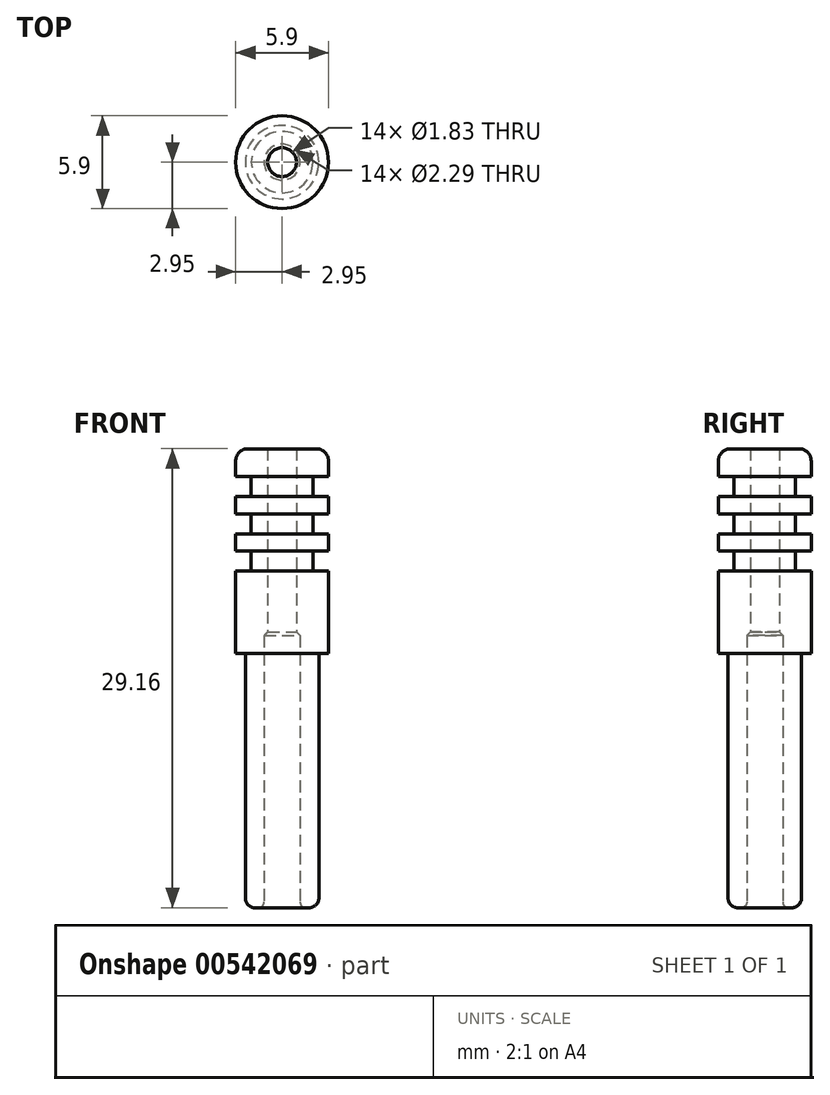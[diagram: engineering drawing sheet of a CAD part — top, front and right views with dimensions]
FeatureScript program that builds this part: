
annotation { "Feature Type Name" : "Feature", "Feature Type Description" : "" }
export const myFeature = defineFeature(function(context is Context, id is Id, definition is map)
    precondition{}
    {
        {
            var Q0;
            Q0=qCreatedBy(makeId("Front.planeOp"),FACE);
            var sketch = newSketch(context, id + "F0", { "sketchPlane" : qUnion([Q0])});
            skLineSegment(sketch, "E0", {"start": v(0.91, 1.37) * mm, "end": v(0.91, 13) * mm});
            skLineSegment(sketch, "E1", {"start": v(0.91, 13) * mm, "end": v(2.18, 13) * mm});
            skLineSegment(sketch, "E2", {"start": v(2.95, 12.24) * mm, "end": v(2.95, 11.25) * mm});
            skLineSegment(sketch, "E3", {"start": v(2.95, 11.25) * mm, "end": v(1.96, 11.25) * mm});
            skLineSegment(sketch, "E4", {"start": v(1.96, 11.25) * mm, "end": v(1.96, 9.98) * mm});
            skLineSegment(sketch, "E5", {"start": v(1.96, 9.98) * mm, "end": v(2.95, 9.98) * mm});
            skLineSegment(sketch, "E6", {"start": v(2.95, 9.98) * mm, "end": v(2.95, 8.86) * mm});
            skLineSegment(sketch, "E7", {"start": v(2.95, 8.87) * mm, "end": v(1.96, 8.87) * mm});
            skLineSegment(sketch, "E8", {"start": v(1.96, 8.87) * mm, "end": v(1.96, 7.6) * mm});
            skLineSegment(sketch, "E9", {"start": v(1.96, 7.6) * mm, "end": v(2.95, 7.6) * mm});
            skLineSegment(sketch, "E10", {"start": v(2.95, 7.6) * mm, "end": v(2.95, 6.5) * mm});
            skLineSegment(sketch, "E11", {"start": v(2.95, 6.5) * mm, "end": v(1.96, 6.5) * mm});
            skLineSegment(sketch, "E12", {"start": v(1.96, 6.5) * mm, "end": v(1.96, 5.23) * mm});
            skLineSegment(sketch, "E13", {"start": v(2.34, 0) * mm, "end": v(2.34, -15.52) * mm});
            skLineSegment(sketch, "E14", {"start": v(1.7, -16.15) * mm, "end": v(1.52, -16.15) * mm});
            skLineSegment(sketch, "E15", {"start": v(1.14, -15.77) * mm, "end": v(1.14, 1.14) * mm});
            skLineSegment(sketch, "E16", {"start": v(1.14, 1.14) * mm, "end": v(0.91, 1.37) * mm});
            skPoint(sketch, "E17.visualSharp", {"position": v(2.95, 13) * mm});
            skArc(sketch, "E17.filletArc", {"start": v(2.95, 12.24) * mm, "mid": v(2.72, 12.78) * mm, "end": v(2.18, 13) * mm});
            skLineSegment(sketch, "E18", {"start": v(1.96, 5.23) * mm, "end": v(2.95, 5.23) * mm});
            skLineSegment(sketch, "E19", {"start": v(2.95, 5.23) * mm, "end": v(2.95, 0) * mm});
            skLineSegment(sketch, "E20", {"start": v(2.95, 0) * mm, "end": v(2.34, 0) * mm});
            skPoint(sketch, "E21.visualSharp", {"position": v(2.34, -16.15) * mm});
            skArc(sketch, "E21.filletArc", {"start": v(1.7, -16.15) * mm, "mid": v(2.15, -15.97) * mm, "end": v(2.34, -15.52) * mm});
            skPoint(sketch, "E22.visualSharp", {"position": v(1.14, -16.15) * mm});
            skArc(sketch, "E22.filletArc", {"start": v(1.14, -15.77) * mm, "mid": v(1.25, -16.04) * mm, "end": v(1.52, -16.15) * mm});
            skLineSegment(sketch, "E23", {"start": v(0, 0) * mm, "end": v(0, 22.51) * mm, "construction": true});
            skSolve(sketch);
        }
        {
            var Q0;
            Q0 = qSketchRegion(id + "F0", true);
            var Q1;
            Q1=sQuery(id+"F0.wireOp",EDGE,"E23");
            revolve(context, id + "F1", {"entities" : qUnion([Q0]), "axis" : qUnion([Q1]), "revolveType" : RevolveType.FULL});
        }
    });
